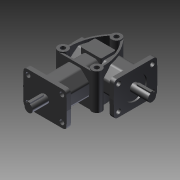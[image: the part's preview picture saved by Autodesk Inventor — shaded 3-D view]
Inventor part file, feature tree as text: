
AUTODESK INVENTOR PART (.ipt)
format: ipt  version: 2011 SP1 (Build 150282100, 282)  size: 404,992 bytes
history: native  units: mm
features: sketch x20, extrude x17, hole x2, revolve x1
ambient origin geometry x8: Origin, YZ Plane, XZ Plane, XY Plane, X Axis, Y Axis, Z Axis, Center Point
bodies: Solid1 (feature_tree)
feature tree (40):
  extrude  "Extrusion1"  TaperAngle=360.0deg  [1 undecoded]
  hole  "Hole1"  [1 undecoded]
  revolve  "Revolution1"  [1 undecoded]
  extrude  "Extrusion2"  Depth=31.0mm TaperAngle=0.0deg
  extrude  "Extrusion3"  Depth=66.0mm TaperAngle=0.0deg
  extrude  "Extrusion4"  Depth=66.0mm TaperAngle=0.0deg
  extrude  "Extrusion5"  Depth=66.0mm TaperAngle=0.0deg
  extrude  "Extrusion6"  Depth=8.0mm TaperAngle=0.0deg
  extrude  "Extrusion7"  Depth=60.0mm TaperAngle=0.0deg
  extrude  "Extrusion8"  [1 undecoded]
  extrude  "Extrusion9"  [1 undecoded]
  extrude  "Extrusion10"  [1 undecoded]
  extrude  "Extrusion11"  [1 undecoded]
  extrude  "Extrusion12"  [1 undecoded]
  extrude  "Extrusion13"  [1 undecoded]
  extrude  "Extrusion14"  [1 undecoded]
  extrude  "Extrusion15"  [1 undecoded]
  hole  "Hole2"  [1 undecoded]
  extrude  "Extrusion16"  [1 undecoded]
  extrude  "Extrusion17"  [1 undecoded]
  sketch  "Sketch_1"  dims[d0=8.0mm d1=0.0mm]
  sketch  "Sketch2"  dims[d2=42.0mm d3=6.0mm d4=4.0mm d5=2.0mm d6=90.0deg d7=3.0mm d8=0.0mm d9=360.0deg]
  sketch  "Sketch_3"  dims[d10=9.5mm d11=0.0mm d12=100.0mm d13=0.0mm]
  sketch  "Sketch_5"  dims[d14=132.0mm d15=0.0mm d16=80.0mm d17=0.0mm]
  sketch  "Sketch_6"  dims[d18=41.0mm d19=0.0mm d20=31.0mm d21=0.0mm]
  sketch  "Sketch_7"  dims[d22=62.0mm d23=0.0mm d24=66.0mm d25=0.0mm]
  sketch  "Sketch_9"  dims[d26=66.0mm d27=0.0mm d28=66.0mm d29=0.0mm]
  sketch  "Sketch_10"  dims[d30=66.0mm d31=0.0mm d32=66.0mm d33=0.0mm]
  sketch  "Sketch_11"  dims[d34=66.0mm d35=0.0mm d36=8.0mm d37=0.0mm]
  sketch  "Sketch_12"  dims[d38=42.0mm d39=6.0mm d40=4.0mm d41=2.0mm d42=90.0deg d43=3.0mm d44=0.0mm d45=60.0mm d46=0.0mm]
  sketch  "Sketch_21"
  sketch  "Sketch_13"  dims[d47=9.5mm d48=0.0mm]
  sketch  "Sketch_22"
  sketch  "Sketch_14"
  sketch  "Sketch_23"
  sketch  "Sketch_15"
  sketch  "Sketch_16"
  sketch  "Sketch18"
  sketch  "Sketch_18"
  sketch  "Sketch_20"
note: 14 required parameter values undecoded (feature->parameter linkage not recoverable at this tier; creation-order binding heuristic only, values carry confidence <= 0.55)